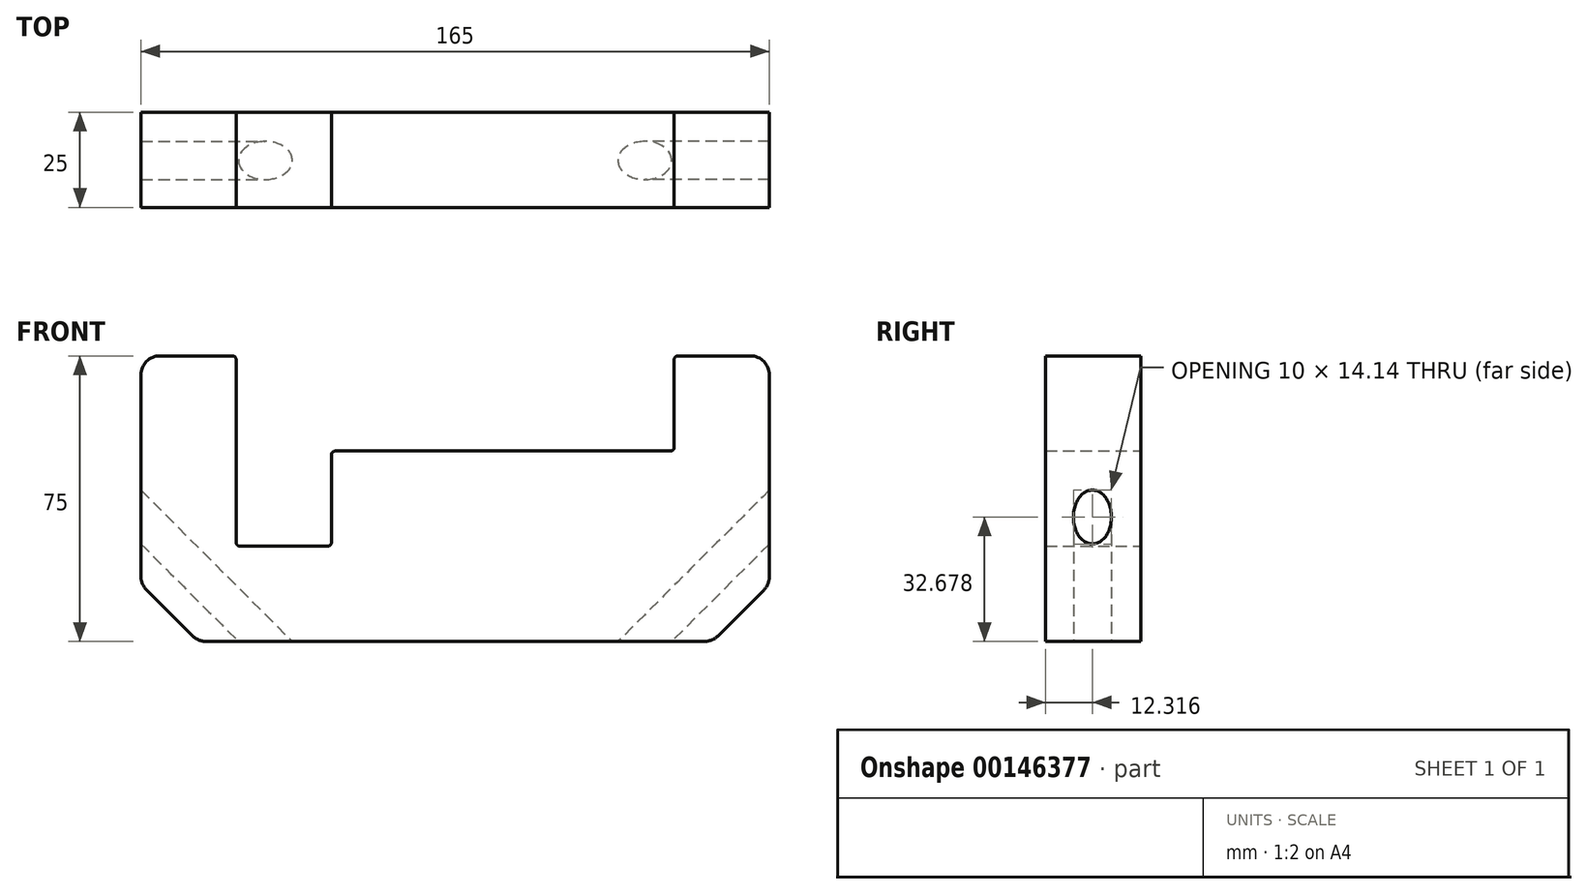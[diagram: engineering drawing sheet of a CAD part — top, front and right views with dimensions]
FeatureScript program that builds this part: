
annotation { "Feature Type Name" : "Feature", "Feature Type Description" : "" }
export const myFeature = defineFeature(function(context is Context, id is Id, definition is map)
    precondition{}
    {
        {
            assignVariable(context, id + "F0", {"name" : "cuadrado", "anyValue" : 5});
        }
        {
            assignVariable(context, id + "F1", {"name" : "ancho", "anyValue" : 25});
        }
        {
            var Q0;
            Q0=qCreatedBy(makeId("Front.planeOp"),FACE);
            var sketch = newSketch(context, id + "F2", { "sketchPlane" : qUnion([Q0])});
            skLineSegment(sketch, "E0", {"start": v(78.04, 0) * mm, "end": v(78.04, 75) * mm});
            skLineSegment(sketch, "E1", {"start": v(78.04, 75) * mm, "end": v(53.04, 75) * mm});
            skLineSegment(sketch, "E2", {"start": v(53.04, 75) * mm, "end": v(53.04, 50) * mm});
            skLineSegment(sketch, "E3", {"start": v(53.04, 50) * mm, "end": v(-36.96, 50) * mm});
            skLineSegment(sketch, "E4", {"start": v(-36.96, 50) * mm, "end": v(-36.96, 25) * mm});
            skLineSegment(sketch, "E5", {"start": v(-36.96, 25) * mm, "end": v(-61.96, 25) * mm});
            skLineSegment(sketch, "E6", {"start": v(-61.96, 25) * mm, "end": v(-61.96, 75) * mm});
            skLineSegment(sketch, "E7", {"start": v(-61.96, 75) * mm, "end": v(-86.96, 75) * mm});
            skLineSegment(sketch, "E8", {"start": v(-86.96, 75) * mm, "end": v(-86.96, 0) * mm});
            skLineSegment(sketch, "E9", {"start": v(-86.96, 0) * mm, "end": v(78.04, 0) * mm});
            skSolve(sketch);
        }
        {
            var Q0;
            Q0=makeQuery(id+"F2.imprint","IMPRINT",FACE,{"disambiguationData":[TD([[makeQuery(id+"F2.imprint","IMPRINT",EDGE,{"derivedFrom":sQuery(id+"F2.wireOp",EDGE,"E0")}),1.0]])]});
            extrude(context, id + "F3", {"entities" : qUnion([Q0]), "depth" : (getVariable(context, 'ancho')) * mm});
        }
        {
            var Q0;
            Q0=makeQuery(id+"F3.opExtrude","SWEPT_EDGE",EDGE,{"disambiguationData":[OSD([sQuery(id+"F2.wireOp",EDGE,"E0"),sQuery(id+"F2.wireOp",EDGE,"E9")])]});
            chamfer(context, id + "F4", {"entities" : qUnion([Q0]), "width" : getVariable(context, 'cuadrado') * 3 * mm, "tangentPropagation" : true});
        }
        {
            var Q0;
            Q0=makeQuery(id+"F3.opExtrude","SWEPT_EDGE",EDGE,{"disambiguationData":[OSD([sQuery(id+"F2.wireOp",EDGE,"E8"),sQuery(id+"F2.wireOp",EDGE,"E9")])]});
            chamfer(context, id + "F5", {"entities" : qUnion([Q0]), "width" : getVariable(context, 'cuadrado') * 3 * mm});
        }
        {
            var Q0;
            Q0=makeQuery(id+"F5.opChamfer","BLEND_FACE",FACE,{"disambiguationData":[OSD([sQuery(id+"F2.wireOp",EDGE,"E8"),sQuery(id+"F2.wireOp",EDGE,"E9")])]});
            cPlane(context, id + "F6", {"entities" : qUnion([Q0]), "cplaneType" : CPlaneType.OFFSET, "offset" : getVariable(context, 'ancho') / 2 * mm, "oppositeDirection" : true, "width" : 150 * mm, "height" : 150 * mm});
        }
        {
            var Q0;
            Q0=qCreatedBy(id+"F6.planeOp",FACE);
            var sketch = newSketch(context, id + "F7", { "sketchPlane" : qUnion([Q0])});
            skLineSegment(sketch, "E10", {"start": v(12.68, 128.86) * mm, "end": v(12.68, 38.86) * mm, "construction": true});
            skSolve(sketch);
        }
        {
            var Q0;
            Q0=qCreatedBy(id+"F6.planeOp",FACE);
            var sketch = newSketch(context, id + "F8", { "sketchPlane" : qUnion([Q0])});
            skLineSegment(sketch, "E11.bottom", {"start": v(12.68, 99.24) * mm, "end": v(17.68, 99.24) * mm});
            skLineSegment(sketch, "E11.top", {"start": v(12.68, 26.14) * mm, "end": v(17.68, 26.14) * mm});
            skLineSegment(sketch, "E11.left", {"start": v(12.68, 99.24) * mm, "end": v(12.68, 26.14) * mm});
            skLineSegment(sketch, "E11.right", {"start": v(17.68, 99.24) * mm, "end": v(17.68, 26.14) * mm});
            skSolve(sketch);
        }
        {
            var Q0;
            Q0 = qSketchRegion(id + "F8", true);
            var Q1;
            Q1=sQuery(id+"F7.wireOp",EDGE,"E10");
            revolve(context, id + "F9", {"operationType" : NewBodyOperationType.REMOVE, "entities" : qUnion([Q0]), "axis" : qUnion([Q1]), "revolveType" : RevolveType.FULL, "oppositeDirection" : true});
        }
        {
            var Q0;
            Q0=makeQuery(id+"F4.opChamfer","BLEND_FACE",FACE,{"disambiguationData":[OSD([sQuery(id+"F2.wireOp",EDGE,"E0"),sQuery(id+"F2.wireOp",EDGE,"E9")])]});
            cPlane(context, id + "F10", {"entities" : qUnion([Q0]), "cplaneType" : CPlaneType.OFFSET, "offset" : getVariable(context, 'ancho') / 2 * mm, "oppositeDirection" : true, "width" : 150 * mm, "height" : 150 * mm});
        }
        {
            var Q0;
            Q0=qCreatedBy(id+"F10.planeOp",FACE);
            var sketch = newSketch(context, id + "F11", { "sketchPlane" : qUnion([Q0])});
            skLineSegment(sketch, "E12", {"start": v(-12.68, 16.12) * mm, "end": v(-12.68, 123) * mm, "construction": true});
            skSolve(sketch);
        }
        {
            var Q0;
            Q0=qCreatedBy(id+"F10.planeOp",FACE);
            var sketch = newSketch(context, id + "F12", { "sketchPlane" : qUnion([Q0])});
            skLineSegment(sketch, "E13.bottom", {"start": v(-7.68, 19.88) * mm, "end": v(-12.68, 19.88) * mm});
            skLineSegment(sketch, "E13.top", {"start": v(-7.68, 89.88) * mm, "end": v(-12.68, 89.88) * mm});
            skLineSegment(sketch, "E13.left", {"start": v(-7.68, 19.88) * mm, "end": v(-7.68, 89.88) * mm});
            skLineSegment(sketch, "E13.right", {"start": v(-12.68, 19.88) * mm, "end": v(-12.68, 89.88) * mm});
            skSolve(sketch);
        }
        {
            var Q0;
            Q0 = qSketchRegion(id + "F12", true);
            var Q1;
            Q1=sQuery(id+"F11.wireOp",EDGE,"E12");
            revolve(context, id + "F13", {"operationType" : NewBodyOperationType.REMOVE, "entities" : qUnion([Q0]), "axis" : qUnion([Q1]), "revolveType" : RevolveType.FULL});
        }
        {
            var Q0;
            Q0=makeQuery(id+"F3.opExtrude","SWEPT_EDGE",EDGE,{"disambiguationData":[OSD([sQuery(id+"F2.wireOp",EDGE,"E3"),sQuery(id+"F2.wireOp",EDGE,"E4")])]});
            var Q1;
            Q1=makeQuery(id+"F3.opExtrude","SWEPT_EDGE",EDGE,{"disambiguationData":[OSD([sQuery(id+"F2.wireOp",EDGE,"E4"),sQuery(id+"F2.wireOp",EDGE,"E5")])]});
            var Q2;
            Q2=makeQuery(id+"F3.opExtrude","SWEPT_EDGE",EDGE,{"disambiguationData":[OSD([sQuery(id+"F2.wireOp",EDGE,"E5"),sQuery(id+"F2.wireOp",EDGE,"E6")])]});
            var Q3;
            Q3=makeQuery(id+"F3.opExtrude","SWEPT_EDGE",EDGE,{"disambiguationData":[OSD([sQuery(id+"F2.wireOp",EDGE,"E1"),sQuery(id+"F2.wireOp",EDGE,"E2")])]});
            var Q4;
            Q4=makeQuery(id+"F3.opExtrude","SWEPT_EDGE",EDGE,{"disambiguationData":[OSD([sQuery(id+"F2.wireOp",EDGE,"E2"),sQuery(id+"F2.wireOp",EDGE,"E3")])]});
            var Q5;
            Q5=makeQuery(id+"F3.opExtrude","SWEPT_EDGE",EDGE,{"disambiguationData":[OSD([sQuery(id+"F2.wireOp",EDGE,"E6"),sQuery(id+"F2.wireOp",EDGE,"E7")])]});
            fillet(context, id + "F14", {"entities" : qUnion([Q0, Q1, Q2, Q3, Q4, Q5]), "radius" : 1 * mm, "tangentPropagation" : true, "allowEdgeOverflow" : false});
        }
        {
            var Q0;
            Q0=makeQuery(id+"F3.opExtrude","SWEPT_EDGE",EDGE,{"disambiguationData":[OSD([sQuery(id+"F2.wireOp",EDGE,"E0"),sQuery(id+"F2.wireOp",EDGE,"E1")])]});
            var Q1;
            Q1=makeQuery(id+"F3.opExtrude","SWEPT_EDGE",EDGE,{"disambiguationData":[OSD([sQuery(id+"F2.wireOp",EDGE,"E7"),sQuery(id+"F2.wireOp",EDGE,"E8")])]});
            fillet(context, id + "F15", {"entities" : qUnion([Q0, Q1]), "radius" : 5 * mm, "tangentPropagation" : true, "allowEdgeOverflow" : false});
        }
        {
            var Q0;
            {var subQ0=sQuery(id+"F2.wireOp",EDGE,"E9");Q0=makeQuery(id+"F4.opChamfer","BLEND_EDGE",EDGE,{"blendedFrom":[makeQuery(id+"F3.opExtrude","SWEPT_EDGE",EDGE,{"disambiguationData":[OSD([sQuery(id+"F2.wireOp",EDGE,"E0"),subQ0])]}),makeQuery(id+"F3.opExtrude","SWEPT_FACE",FACE,{"disambiguationData":[OSD([subQ0])]})],"blendedInto":[makeQuery(id+"F3.opExtrude","SWEPT_FACE",FACE,{"disambiguationData":[OSD([subQ0])]})]});}
            fillet(context, id + "F16", {"entities" : qUnion([Q0]), "radius" : 5 * mm, "tangentPropagation" : true, "allowEdgeOverflow" : false});
        }
        {
            var Q0;
            {var subQ0=sQuery(id+"F2.wireOp",EDGE,"E0");Q0=makeQuery(id+"F4.opChamfer","BLEND_EDGE",EDGE,{"blendedFrom":[makeQuery(id+"F3.opExtrude","SWEPT_EDGE",EDGE,{"disambiguationData":[OSD([subQ0,sQuery(id+"F2.wireOp",EDGE,"E9")])]}),makeQuery(id+"F3.opExtrude","SWEPT_FACE",FACE,{"disambiguationData":[OSD([subQ0])]})],"blendedInto":[makeQuery(id+"F3.opExtrude","SWEPT_FACE",FACE,{"disambiguationData":[OSD([subQ0])]})]});}
            fillet(context, id + "F17", {"entities" : qUnion([Q0]), "radius" : 5 * mm, "tangentPropagation" : true, "allowEdgeOverflow" : false});
        }
        {
            var Q0;
            {var subQ0=sQuery(id+"F2.wireOp",EDGE,"E9");Q0=makeQuery(id+"F5.opChamfer","BLEND_EDGE",EDGE,{"blendedFrom":[makeQuery(id+"F3.opExtrude","SWEPT_EDGE",EDGE,{"disambiguationData":[OSD([sQuery(id+"F2.wireOp",EDGE,"E8"),subQ0])]}),makeQuery(id+"F3.opExtrude","SWEPT_FACE",FACE,{"disambiguationData":[OSD([subQ0])]})],"blendedInto":[makeQuery(id+"F3.opExtrude","SWEPT_FACE",FACE,{"disambiguationData":[OSD([subQ0])]})]});}
            fillet(context, id + "F18", {"entities" : qUnion([Q0]), "radius" : 5 * mm, "tangentPropagation" : true, "allowEdgeOverflow" : false});
        }
        {
            var Q0;
            {var subQ0=sQuery(id+"F2.wireOp",EDGE,"E8");Q0=makeQuery(id+"F5.opChamfer","BLEND_EDGE",EDGE,{"blendedFrom":[makeQuery(id+"F3.opExtrude","SWEPT_EDGE",EDGE,{"disambiguationData":[OSD([subQ0,sQuery(id+"F2.wireOp",EDGE,"E9")])]}),makeQuery(id+"F3.opExtrude","SWEPT_FACE",FACE,{"disambiguationData":[OSD([subQ0])]})],"blendedInto":[makeQuery(id+"F3.opExtrude","SWEPT_FACE",FACE,{"disambiguationData":[OSD([subQ0])]})]});}
            fillet(context, id + "F19", {"entities" : qUnion([Q0]), "radius" : 5 * mm, "tangentPropagation" : true, "allowEdgeOverflow" : false});
        }
    });
